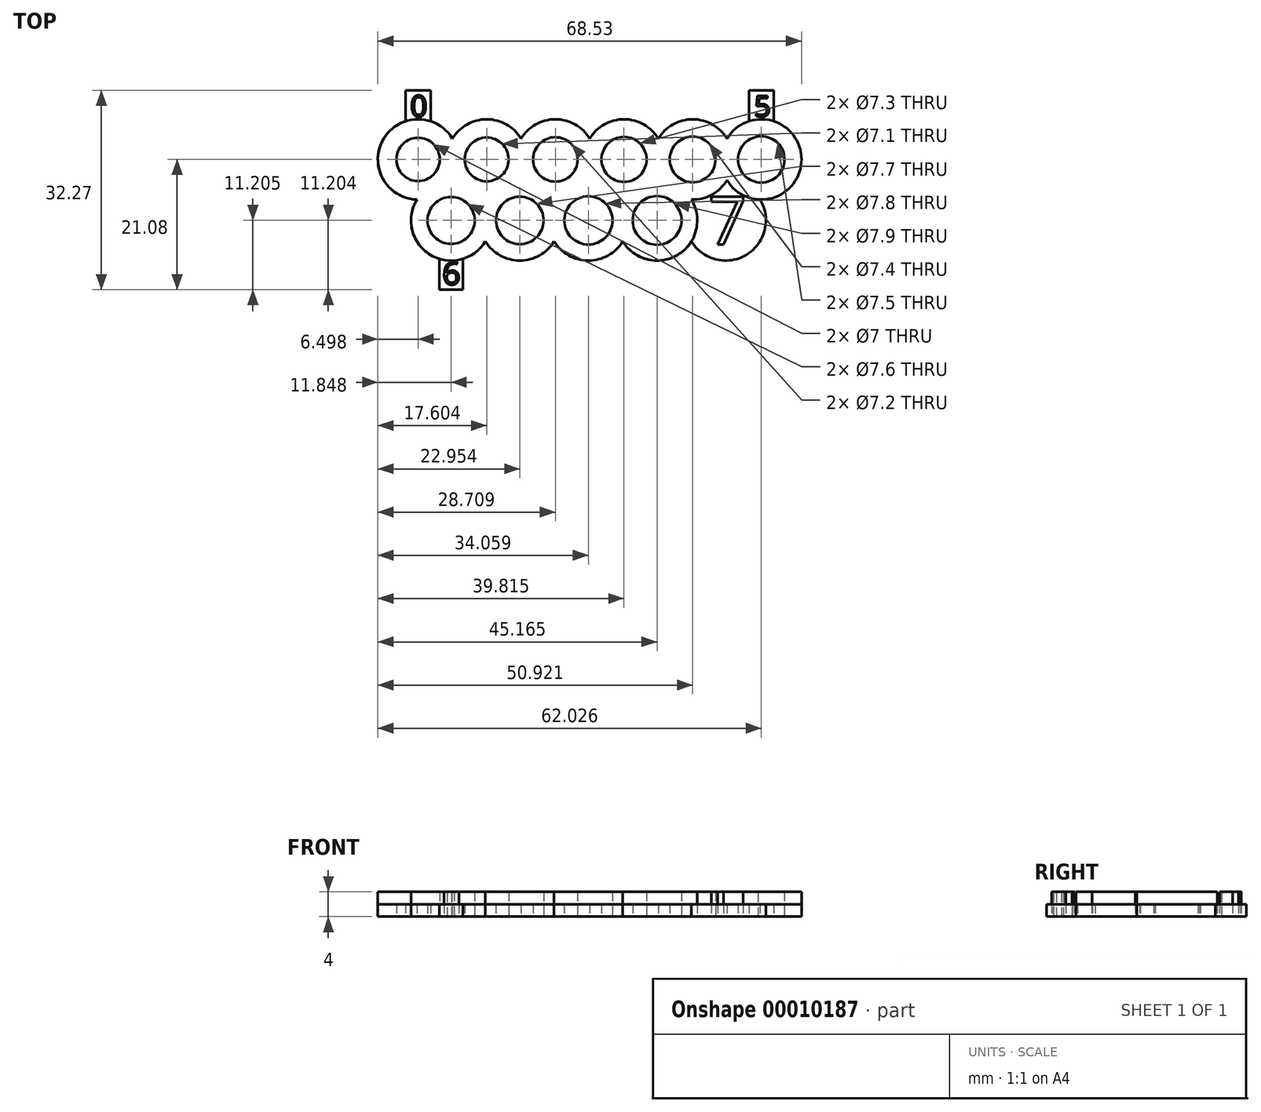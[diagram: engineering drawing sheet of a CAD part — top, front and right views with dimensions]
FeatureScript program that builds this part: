
annotation { "Feature Type Name" : "Feature", "Feature Type Description" : "" }
export const myFeature = defineFeature(function(context is Context, id is Id, definition is map)
    precondition{}
    {
        {
            var Q0;
            Q0=qCreatedBy(makeId("Top.planeOp"),FACE);
            var sketch = newSketch(context, id + "F0", { "sketchPlane" : qUnion([Q0])});
            skCircle(sketch, "E0", {"center": v(-32.25, 0) * mm, "radius": 6.5 * mm});
            skCircle(sketch, "E1", {"center": v(-32.25, 0) * mm, "radius": 3.5 * mm});
            skCircle(sketch, "E2", {"center": v(-21.15, 0) * mm, "radius": 6.5 * mm});
            skCircle(sketch, "E3", {"center": v(-21.15, 0) * mm, "radius": 3.55 * mm});
            skCircle(sketch, "E4", {"center": v(-10.04, 0) * mm, "radius": 6.5 * mm});
            skCircle(sketch, "E5", {"center": v(-10.04, 0) * mm, "radius": 3.6 * mm});
            skCircle(sketch, "E6", {"center": v(1.07, 0) * mm, "radius": 6.5 * mm});
            skCircle(sketch, "E7", {"center": v(1.07, 0) * mm, "radius": 3.65 * mm});
            skCircle(sketch, "E8", {"center": v(12.17, 0) * mm, "radius": 6.5 * mm});
            skCircle(sketch, "E9", {"center": v(12.17, 0) * mm, "radius": 3.7 * mm});
            skCircle(sketch, "E10", {"center": v(23.28, 0) * mm, "radius": 6.5 * mm});
            skCircle(sketch, "E11", {"center": v(23.28, 0) * mm, "radius": 3.75 * mm});
            skCircle(sketch, "E12", {"center": v(-26.9, -9.88) * mm, "radius": 6.5 * mm});
            skCircle(sketch, "E13", {"center": v(-26.9, -9.88) * mm, "radius": 3.8 * mm});
            skCircle(sketch, "E14", {"center": v(-15.8, -9.88) * mm, "radius": 6.5 * mm});
            skCircle(sketch, "E15", {"center": v(-15.8, -9.88) * mm, "radius": 3.85 * mm});
            skCircle(sketch, "E16", {"center": v(-4.7, -9.88) * mm, "radius": 6.5 * mm});
            skCircle(sketch, "E17", {"center": v(-4.7, -9.88) * mm, "radius": 3.9 * mm});
            skCircle(sketch, "E18", {"center": v(6.42, -9.88) * mm, "radius": 6.5 * mm});
            skCircle(sketch, "E19", {"center": v(6.42, -9.88) * mm, "radius": 3.95 * mm});
            skCircle(sketch, "E20", {"center": v(17.52, -9.88) * mm, "radius": 6.5 * mm});
            skPoint(sketch, "E21", {"position": v(-26.7, -3.38) * mm});
            skPoint(sketch, "E22", {"position": v(-15.6, -3.38) * mm});
            skPoint(sketch, "E23", {"position": v(-21.35, -6.5) * mm});
            skPoint(sketch, "E24", {"position": v(-10.24, -6.5) * mm});
            skPoint(sketch, "E25", {"position": v(-4.49, -3.38) * mm});
            skPoint(sketch, "E26", {"position": v(0.86, -6.5) * mm});
            skPoint(sketch, "E27", {"position": v(6.62, -3.38) * mm});
            skPoint(sketch, "E28", {"position": v(11.97, -6.5) * mm});
            skPoint(sketch, "E29", {"position": v(17.72, -3.38) * mm});
            skLineSegment(sketch, "E30.bottom", {"start": v(-34.27, 6.18) * mm, "end": v(-30.23, 6.18) * mm});
            skLineSegment(sketch, "E30.top", {"start": v(-34.27, 11.18) * mm, "end": v(-30.23, 11.18) * mm});
            skLineSegment(sketch, "E30.left", {"start": v(-34.27, 6.18) * mm, "end": v(-34.27, 11.18) * mm});
            skLineSegment(sketch, "E30.right", {"start": v(-30.23, 6.18) * mm, "end": v(-30.23, 11.18) * mm});
            skText(sketch, "E31", { "text": "0", "fontName": "OpenSans-Regular.ttf"});
            skLineSegment(sketch, "E32.left", {"start": v(21.3, 6.19) * mm, "end": v(21.3, 11.19) * mm});
            skLineSegment(sketch, "E32.bottom", {"start": v(21.3, 6.19) * mm, "end": v(25.26, 6.19) * mm});
            skLineSegment(sketch, "E32.right", {"start": v(25.26, 6.19) * mm, "end": v(25.26, 11.19) * mm});
            skLineSegment(sketch, "E32.top", {"start": v(21.3, 11.19) * mm, "end": v(25.26, 11.19) * mm});
            skText(sketch, "E33", { "text": "5", "fontName": "OpenSans-Regular.ttf"});
            skLineSegment(sketch, "E34.left", {"start": v(-28.83, -21.08) * mm, "end": v(-28.83, -16.08) * mm});
            skLineSegment(sketch, "E34.bottom", {"start": v(-28.83, -21.08) * mm, "end": v(-24.97, -21.08) * mm});
            skLineSegment(sketch, "E34.right", {"start": v(-24.97, -21.08) * mm, "end": v(-24.97, -16.08) * mm});
            skLineSegment(sketch, "E34.top", {"start": v(-28.83, -16.08) * mm, "end": v(-24.97, -16.08) * mm});
            skText(sketch, "E35", { "text": "6", "fontName": "OpenSans-Regular.ttf"});
            skText(sketch, "E36", { "text": "7", "fontName": "OpenSans-Regular.ttf"});
            skLineSegment(sketch, "E37", {"start": v(-26.9, -9.88) * mm, "end": v(17.52, -9.88) * mm, "construction": true});
            const initialGuessF0  = {"E31": [-0.0335, 0.00693, 1, 0, 0.00343], "E33": [0.02213, 0.00693, 1, 0, 0.00336], "E35": [-0.02832, -0.02026, 1, 0, 0.00367], "E36": [0.0147, -0.01377, 1, 0, 0.00778]};
            skSetInitialGuess(sketch, initialGuessF0);
            skSolve(sketch);
        }
        {
            var Q0;
            Q0=makeQuery(id+"F0.imprint","IMPRINT",FACE,{"disambiguationData":[TD([[makeQuery(id+"F0.imprint","IMPRINT",EDGE,{"derivedFrom":sQuery(id+"F0.wireOp",EDGE,"E11")}),-1.0]])]});
            var Q1;
            {var subQ0=sQuery(id+"F0.wireOp",EDGE,"E16");var subQ1=sQuery(id+"F0.wireOp",EDGE,"E4");var subQ3=makeQuery(id+"F0.imprint","INTERSECT",VERTEX,{"derivedFrom":[subQ1,sQuery(id+"F0.wireOp",EDGE,"E14"),subQ0]});Q1=makeQuery(id+"F0.imprint","IMPRINT",FACE,{"disambiguationData":[TD([[makeQuery(id+"F0.imprint","IMPRINT",EDGE,{"disambiguationData":[TD([[subQ3,-1.0]])],"derivedFrom":subQ1}),1.0]])]});}
            var Q2;
            {var subQ0=sQuery(id+"F0.wireOp",EDGE,"E18");var subQ1=sQuery(id+"F0.wireOp",EDGE,"E6");var subQ3=makeQuery(id+"F0.imprint","INTERSECT",VERTEX,{"derivedFrom":[subQ1,sQuery(id+"F0.wireOp",EDGE,"E16"),subQ0]});Q2=makeQuery(id+"F0.imprint","IMPRINT",FACE,{"disambiguationData":[TD([[makeQuery(id+"F0.imprint","IMPRINT",EDGE,{"disambiguationData":[TD([[subQ3,-1.0]])],"derivedFrom":subQ1}),1.0]])]});}
            var Q3;
            Q3=makeQuery(id+"F0.imprint","IMPRINT",FACE,{"disambiguationData":[TD([[makeQuery(id+"F0.imprint","IMPRINT",EDGE,{"derivedFrom":sQuery(id+"F0.wireOp",EDGE,"E33.sketch_text.stroke-0")}),-1.0]])]});
            var Q4;
            {var subQ0=sQuery(id+"F0.wireOp",EDGE,"E6");var subQ1=sQuery(id+"F0.wireOp",EDGE,"E4");var subQ3=makeQuery(id+"F0.imprint","INTERSECT",VERTEX,{"derivedFrom":[subQ1,subQ0]});Q4=makeQuery(id+"F0.imprint","IMPRINT",FACE,{"disambiguationData":[TD([[makeQuery(id+"F0.imprint","IMPRINT",EDGE,{"disambiguationData":[TD([[subQ3,1.0]])],"derivedFrom":subQ1}),1.0]])]});}
            var Q5;
            {var subQ0=sQuery(id+"F0.wireOp",EDGE,"E10");var subQ1=sQuery(id+"F0.wireOp",EDGE,"E8");var subQ3=makeQuery(id+"F0.imprint","INTERSECT",VERTEX,{"derivedFrom":[subQ1,subQ0]});Q5=makeQuery(id+"F0.imprint","IMPRINT",FACE,{"disambiguationData":[TD([[makeQuery(id+"F0.imprint","IMPRINT",EDGE,{"disambiguationData":[TD([[subQ3,1.0]])],"derivedFrom":subQ1}),1.0]])]});}
            var Q6;
            {var subQ0=sQuery(id+"F0.wireOp",EDGE,"E12");var subQ1=sQuery(id+"F0.wireOp",EDGE,"E2");var subQ3=makeQuery(id+"F0.imprint","INTERSECT",VERTEX,{"derivedFrom":[sQuery(id+"F0.wireOp",EDGE,"E0"),subQ1,subQ0]});Q6=makeQuery(id+"F0.imprint","IMPRINT",FACE,{"disambiguationData":[TD([[makeQuery(id+"F0.imprint","IMPRINT",EDGE,{"disambiguationData":[TD([[subQ3,-1.0]])],"derivedFrom":subQ1}),1.0]])]});}
            var Q7;
            {var subQ0=sQuery(id+"F0.wireOp",EDGE,"E14");var subQ1=sQuery(id+"F0.wireOp",EDGE,"E12");var subQ3=makeQuery(id+"F0.imprint","INTERSECT",VERTEX,{"derivedFrom":[subQ1,subQ0]});Q7=makeQuery(id+"F0.imprint","IMPRINT",FACE,{"disambiguationData":[TD([[makeQuery(id+"F0.imprint","IMPRINT",EDGE,{"disambiguationData":[TD([[subQ3,-1.0]])],"derivedFrom":subQ1}),1.0]])]});}
            var Q8;
            {var subQ0=sQuery(id+"F0.wireOp",EDGE,"E4");var subQ1=sQuery(id+"F0.wireOp",EDGE,"E2");var subQ3=makeQuery(id+"F0.imprint","INTERSECT",VERTEX,{"derivedFrom":[subQ1,subQ0]});Q8=makeQuery(id+"F0.imprint","IMPRINT",FACE,{"disambiguationData":[TD([[makeQuery(id+"F0.imprint","IMPRINT",EDGE,{"disambiguationData":[TD([[subQ3,1.0]])],"derivedFrom":subQ1}),1.0]])]});}
            var Q9;
            Q9=makeQuery(id+"F0.imprint","IMPRINT",FACE,{"disambiguationData":[TD([[makeQuery(id+"F0.imprint","IMPRINT",EDGE,{"derivedFrom":sQuery(id+"F0.wireOp",EDGE,"E19")}),-1.0]])]});
            var Q10;
            Q10=makeQuery(id+"F0.imprint","IMPRINT",FACE,{"disambiguationData":[TD([[makeQuery(id+"F0.imprint","IMPRINT",EDGE,{"derivedFrom":sQuery(id+"F0.wireOp",EDGE,"E7")}),-1.0]])]});
            var Q11;
            {var subQ0=sQuery(id+"F0.wireOp",EDGE,"E2");var subQ1=sQuery(id+"F0.wireOp",EDGE,"E0");var subQ3=makeQuery(id+"F0.imprint","INTERSECT",VERTEX,{"derivedFrom":[subQ1,subQ0]});Q11=makeQuery(id+"F0.imprint","IMPRINT",FACE,{"disambiguationData":[TD([[makeQuery(id+"F0.imprint","IMPRINT",EDGE,{"disambiguationData":[TD([[subQ3,1.0]])],"derivedFrom":subQ1}),1.0]])]});}
            var Q12;
            Q12=makeQuery(id+"F0.imprint","IMPRINT",FACE,{"disambiguationData":[TD([[makeQuery(id+"F0.imprint","IMPRINT",EDGE,{"derivedFrom":sQuery(id+"F0.wireOp",EDGE,"E36.sketch_text.stroke-0")}),-1.0]])]});
            var Q13;
            {var subQ0=sQuery(id+"F0.wireOp",EDGE,"E20");var subQ1=sQuery(id+"F0.wireOp",EDGE,"E8");var subQ3=makeQuery(id+"F0.imprint","INTERSECT",VERTEX,{"derivedFrom":[subQ1,sQuery(id+"F0.wireOp",EDGE,"E18"),subQ0]});Q13=makeQuery(id+"F0.imprint","IMPRINT",FACE,{"disambiguationData":[TD([[makeQuery(id+"F0.imprint","IMPRINT",EDGE,{"disambiguationData":[TD([[subQ3,-1.0]])],"derivedFrom":subQ1}),1.0]])]});}
            var Q14;
            Q14=makeQuery(id+"F0.imprint","IMPRINT",FACE,{"disambiguationData":[TD([[makeQuery(id+"F0.imprint","IMPRINT",EDGE,{"derivedFrom":sQuery(id+"F0.wireOp",EDGE,"E1")}),-1.0]])]});
            var Q15;
            {var subQ0=sQuery(id+"F0.wireOp",EDGE,"E14");var subQ1=sQuery(id+"F0.wireOp",EDGE,"E4");var subQ3=makeQuery(id+"F0.imprint","INTERSECT",VERTEX,{"derivedFrom":[sQuery(id+"F0.wireOp",EDGE,"E2"),subQ1,subQ0]});Q15=makeQuery(id+"F0.imprint","IMPRINT",FACE,{"disambiguationData":[TD([[makeQuery(id+"F0.imprint","IMPRINT",EDGE,{"disambiguationData":[TD([[subQ3,-1.0]])],"derivedFrom":subQ1}),1.0]])]});}
            var Q16;
            {var subQ0=sQuery(id+"F0.wireOp",EDGE,"E20");var subQ1=sQuery(id+"F0.wireOp",EDGE,"E18");var subQ3=makeQuery(id+"F0.imprint","INTERSECT",VERTEX,{"derivedFrom":[subQ1,subQ0]});Q16=makeQuery(id+"F0.imprint","IMPRINT",FACE,{"disambiguationData":[TD([[makeQuery(id+"F0.imprint","IMPRINT",EDGE,{"disambiguationData":[TD([[subQ3,-1.0]])],"derivedFrom":subQ1}),1.0]])]});}
            var Q17;
            Q17=makeQuery(id+"F0.imprint","IMPRINT",FACE,{"disambiguationData":[TD([[makeQuery(id+"F0.imprint","IMPRINT",EDGE,{"derivedFrom":sQuery(id+"F0.wireOp",EDGE,"E13")}),-1.0]])]});
            var Q18;
            {var subQ0=sQuery(id+"F0.wireOp",EDGE,"E16");var subQ1=sQuery(id+"F0.wireOp",EDGE,"E14");var subQ3=makeQuery(id+"F0.imprint","INTERSECT",VERTEX,{"derivedFrom":[subQ1,subQ0]});Q18=makeQuery(id+"F0.imprint","IMPRINT",FACE,{"disambiguationData":[TD([[makeQuery(id+"F0.imprint","IMPRINT",EDGE,{"disambiguationData":[TD([[subQ3,-1.0]])],"derivedFrom":subQ1}),1.0]])]});}
            var Q19;
            Q19=makeQuery(id+"F0.imprint","IMPRINT",FACE,{"disambiguationData":[TD([[makeQuery(id+"F0.imprint","IMPRINT",EDGE,{"derivedFrom":sQuery(id+"F0.wireOp",EDGE,"E9")}),-1.0]])]});
            var Q20;
            {var subQ0=sQuery(id+"F0.wireOp",EDGE,"E18");var subQ1=sQuery(id+"F0.wireOp",EDGE,"E8");var subQ3=makeQuery(id+"F0.imprint","INTERSECT",VERTEX,{"derivedFrom":[sQuery(id+"F0.wireOp",EDGE,"E6"),subQ1,subQ0]});Q20=makeQuery(id+"F0.imprint","IMPRINT",FACE,{"disambiguationData":[TD([[makeQuery(id+"F0.imprint","IMPRINT",EDGE,{"disambiguationData":[TD([[subQ3,-1.0]])],"derivedFrom":subQ1}),1.0]])]});}
            var Q21;
            Q21=makeQuery(id+"F0.imprint","IMPRINT",FACE,{"disambiguationData":[TD([[makeQuery(id+"F0.imprint","IMPRINT",EDGE,{"derivedFrom":sQuery(id+"F0.wireOp",EDGE,"E3")}),-1.0]])]});
            var Q22;
            {var subQ0=sQuery(id+"F0.wireOp",EDGE,"E18");var subQ1=sQuery(id+"F0.wireOp",EDGE,"E16");var subQ3=makeQuery(id+"F0.imprint","INTERSECT",VERTEX,{"derivedFrom":[subQ1,subQ0]});Q22=makeQuery(id+"F0.imprint","IMPRINT",FACE,{"disambiguationData":[TD([[makeQuery(id+"F0.imprint","IMPRINT",EDGE,{"disambiguationData":[TD([[subQ3,-1.0]])],"derivedFrom":subQ1}),1.0]])]});}
            var Q23;
            {var subQ0=sQuery(id+"F0.wireOp",EDGE,"E8");var subQ1=sQuery(id+"F0.wireOp",EDGE,"E6");var subQ3=makeQuery(id+"F0.imprint","INTERSECT",VERTEX,{"derivedFrom":[subQ1,subQ0]});Q23=makeQuery(id+"F0.imprint","IMPRINT",FACE,{"disambiguationData":[TD([[makeQuery(id+"F0.imprint","IMPRINT",EDGE,{"disambiguationData":[TD([[subQ3,1.0]])],"derivedFrom":subQ1}),1.0]])]});}
            var Q24;
            {var subQ0=sQuery(id+"F0.wireOp",EDGE,"E16");var subQ1=sQuery(id+"F0.wireOp",EDGE,"E6");var subQ3=makeQuery(id+"F0.imprint","INTERSECT",VERTEX,{"derivedFrom":[sQuery(id+"F0.wireOp",EDGE,"E4"),subQ1,subQ0]});Q24=makeQuery(id+"F0.imprint","IMPRINT",FACE,{"disambiguationData":[TD([[makeQuery(id+"F0.imprint","IMPRINT",EDGE,{"disambiguationData":[TD([[subQ3,-1.0]])],"derivedFrom":subQ1}),1.0]])]});}
            var Q25;
            Q25=makeQuery(id+"F0.imprint","IMPRINT",FACE,{"disambiguationData":[TD([[makeQuery(id+"F0.imprint","IMPRINT",EDGE,{"derivedFrom":sQuery(id+"F0.wireOp",EDGE,"E31.sketch_text.stroke-0")}),-1.0]])]});
            var Q26;
            Q26=makeQuery(id+"F0.imprint","IMPRINT",FACE,{"disambiguationData":[TD([[makeQuery(id+"F0.imprint","IMPRINT",EDGE,{"derivedFrom":sQuery(id+"F0.wireOp",EDGE,"E5")}),-1.0]])]});
            var Q27;
            Q27=makeQuery(id+"F0.imprint","IMPRINT",FACE,{"disambiguationData":[TD([[makeQuery(id+"F0.imprint","IMPRINT",EDGE,{"derivedFrom":sQuery(id+"F0.wireOp",EDGE,"E17")}),-1.0]])]});
            var Q28;
            Q28=makeQuery(id+"F0.imprint","IMPRINT",FACE,{"disambiguationData":[TD([[makeQuery(id+"F0.imprint","IMPRINT",EDGE,{"derivedFrom":sQuery(id+"F0.wireOp",EDGE,"E15")}),-1.0]])]});
            var Q29;
            {var subQ0=sQuery(id+"F0.wireOp",EDGE,"E14");var subQ1=sQuery(id+"F0.wireOp",EDGE,"E2");var subQ3=makeQuery(id+"F0.imprint","INTERSECT",VERTEX,{"derivedFrom":[subQ1,sQuery(id+"F0.wireOp",EDGE,"E12"),subQ0]});Q29=makeQuery(id+"F0.imprint","IMPRINT",FACE,{"disambiguationData":[TD([[makeQuery(id+"F0.imprint","IMPRINT",EDGE,{"disambiguationData":[TD([[subQ3,-1.0]])],"derivedFrom":subQ1}),1.0]])]});}
            var Q30;
            {var subQ0=sQuery(id+"F0.wireOp",EDGE,"E20");var subQ1=sQuery(id+"F0.wireOp",EDGE,"E10");var subQ3=makeQuery(id+"F0.imprint","INTERSECT",VERTEX,{"derivedFrom":[subQ1,subQ0]});Q30=makeQuery(id+"F0.imprint","IMPRINT",FACE,{"disambiguationData":[TD([[makeQuery(id+"F0.imprint","IMPRINT",EDGE,{"disambiguationData":[TD([[subQ3,1.0]])],"derivedFrom":subQ1}),1.0]])]});}
            var Q31;
            {var subQ0=sQuery(id+"F0.wireOp",EDGE,"E12");var subQ1=sQuery(id+"F0.wireOp",EDGE,"E0");var subQ3=makeQuery(id+"F0.imprint","INTERSECT",VERTEX,{"derivedFrom":[subQ1,subQ0]});Q31=makeQuery(id+"F0.imprint","IMPRINT",FACE,{"disambiguationData":[TD([[makeQuery(id+"F0.imprint","IMPRINT",EDGE,{"disambiguationData":[TD([[subQ3,-1.0]])],"derivedFrom":subQ1}),1.0]])]});}
            var Q32;
            Q32=makeQuery(id+"F0.imprint","IMPRINT",FACE,{"disambiguationData":[TD([[makeQuery(id+"F0.imprint","IMPRINT",EDGE,{"derivedFrom":sQuery(id+"F0.wireOp",EDGE,"E35.sketch_text.stroke-0")}),-1.0]])]});
            var Q33;
            {var subQ0=sQuery(id+"F0.wireOp",EDGE,"E34.top");Q33=makeQuery(id+"F0.imprint","IMPRINT",FACE,{"disambiguationData":[TD([[makeQuery(id+"F0.imprint","IMPRINT",EDGE,{"derivedFrom":subQ0}),-1.0]])]});}
            var Q34;
            {var subQ0=sQuery(id+"F0.wireOp",EDGE,"E30.bottom");Q34=makeQuery(id+"F0.imprint","IMPRINT",FACE,{"disambiguationData":[TD([[makeQuery(id+"F0.imprint","IMPRINT",EDGE,{"derivedFrom":subQ0}),1.0]])]});}
            var Q35;
            {var subQ0=sQuery(id+"F0.wireOp",EDGE,"E32.bottom");Q35=makeQuery(id+"F0.imprint","IMPRINT",FACE,{"disambiguationData":[TD([[makeQuery(id+"F0.imprint","IMPRINT",EDGE,{"derivedFrom":subQ0}),1.0]])]});}
            extrude(context, id + "F1", {"entities" : qUnion([Q0, Q1, Q2, Q3, Q4, Q5, Q6, Q7, Q8, Q9, Q10, Q11, Q12, Q13, Q14, Q15, Q16, Q17, Q18, Q19, Q20, Q21, Q22, Q23, Q24, Q25, Q26, Q27, Q28, Q29, Q30, Q31, Q32, Q33, Q34, Q35]), "depth" : 4 * mm});
        }
        {
            var Q0;
            Q0=makeQuery(id+"F0.imprint","IMPRINT",FACE,{"disambiguationData":[TD([[makeQuery(id+"F0.imprint","IMPRINT",EDGE,{"derivedFrom":sQuery(id+"F0.wireOp",EDGE,"E13")}),-1.0]])]});
            var Q1;
            {var subQ0=sQuery(id+"F0.wireOp",EDGE,"E16");var subQ1=sQuery(id+"F0.wireOp",EDGE,"E6");var subQ3=makeQuery(id+"F0.imprint","INTERSECT",VERTEX,{"derivedFrom":[sQuery(id+"F0.wireOp",EDGE,"E4"),subQ1,subQ0]});Q1=makeQuery(id+"F0.imprint","IMPRINT",FACE,{"disambiguationData":[TD([[makeQuery(id+"F0.imprint","IMPRINT",EDGE,{"disambiguationData":[TD([[subQ3,-1.0]])],"derivedFrom":subQ1}),1.0]])]});}
            var Q2;
            {var subQ0=sQuery(id+"F0.wireOp",EDGE,"E8");var subQ1=sQuery(id+"F0.wireOp",EDGE,"E6");var subQ3=makeQuery(id+"F0.imprint","INTERSECT",VERTEX,{"derivedFrom":[subQ1,subQ0]});Q2=makeQuery(id+"F0.imprint","IMPRINT",FACE,{"disambiguationData":[TD([[makeQuery(id+"F0.imprint","IMPRINT",EDGE,{"disambiguationData":[TD([[subQ3,1.0]])],"derivedFrom":subQ1}),1.0]])]});}
            var Q3;
            {var subQ0=sQuery(id+"F0.wireOp",EDGE,"E18");var subQ1=sQuery(id+"F0.wireOp",EDGE,"E6");var subQ3=makeQuery(id+"F0.imprint","INTERSECT",VERTEX,{"derivedFrom":[subQ1,sQuery(id+"F0.wireOp",EDGE,"E16"),subQ0]});Q3=makeQuery(id+"F0.imprint","IMPRINT",FACE,{"disambiguationData":[TD([[makeQuery(id+"F0.imprint","IMPRINT",EDGE,{"disambiguationData":[TD([[subQ3,-1.0]])],"derivedFrom":subQ1}),1.0]])]});}
            var Q4;
            {var subQ0=sQuery(id+"F0.wireOp",EDGE,"E14");var subQ1=sQuery(id+"F0.wireOp",EDGE,"E2");var subQ3=makeQuery(id+"F0.imprint","INTERSECT",VERTEX,{"derivedFrom":[subQ1,sQuery(id+"F0.wireOp",EDGE,"E12"),subQ0]});Q4=makeQuery(id+"F0.imprint","IMPRINT",FACE,{"disambiguationData":[TD([[makeQuery(id+"F0.imprint","IMPRINT",EDGE,{"disambiguationData":[TD([[subQ3,-1.0]])],"derivedFrom":subQ1}),1.0]])]});}
            var Q5;
            Q5=makeQuery(id+"F0.imprint","IMPRINT",FACE,{"disambiguationData":[TD([[makeQuery(id+"F0.imprint","IMPRINT",EDGE,{"derivedFrom":sQuery(id+"F0.wireOp",EDGE,"E1")}),-1.0]])]});
            var Q6;
            Q6=makeQuery(id+"F0.imprint","IMPRINT",FACE,{"disambiguationData":[TD([[makeQuery(id+"F0.imprint","IMPRINT",EDGE,{"derivedFrom":sQuery(id+"F0.wireOp",EDGE,"E11")}),-1.0]])]});
            var Q7;
            {var subQ0=sQuery(id+"F0.wireOp",EDGE,"E16");var subQ1=sQuery(id+"F0.wireOp",EDGE,"E4");var subQ3=makeQuery(id+"F0.imprint","INTERSECT",VERTEX,{"derivedFrom":[subQ1,sQuery(id+"F0.wireOp",EDGE,"E14"),subQ0]});Q7=makeQuery(id+"F0.imprint","IMPRINT",FACE,{"disambiguationData":[TD([[makeQuery(id+"F0.imprint","IMPRINT",EDGE,{"disambiguationData":[TD([[subQ3,-1.0]])],"derivedFrom":subQ1}),1.0]])]});}
            var Q8;
            Q8=makeQuery(id+"F0.imprint","IMPRINT",FACE,{"disambiguationData":[TD([[makeQuery(id+"F0.imprint","IMPRINT",EDGE,{"derivedFrom":sQuery(id+"F0.wireOp",EDGE,"E36.sketch_text.stroke-0")}),1.0]])]});
            var Q9;
            {var subQ0=sQuery(id+"F0.wireOp",EDGE,"E18");var subQ1=sQuery(id+"F0.wireOp",EDGE,"E16");var subQ3=makeQuery(id+"F0.imprint","INTERSECT",VERTEX,{"derivedFrom":[subQ1,subQ0]});Q9=makeQuery(id+"F0.imprint","IMPRINT",FACE,{"disambiguationData":[TD([[makeQuery(id+"F0.imprint","IMPRINT",EDGE,{"disambiguationData":[TD([[subQ3,-1.0]])],"derivedFrom":subQ1}),1.0]])]});}
            var Q10;
            Q10=makeQuery(id+"F0.imprint","IMPRINT",FACE,{"disambiguationData":[TD([[makeQuery(id+"F0.imprint","IMPRINT",EDGE,{"derivedFrom":sQuery(id+"F0.wireOp",EDGE,"E9")}),-1.0]])]});
            var Q11;
            Q11=makeQuery(id+"F0.imprint","IMPRINT",FACE,{"disambiguationData":[TD([[makeQuery(id+"F0.imprint","IMPRINT",EDGE,{"derivedFrom":sQuery(id+"F0.wireOp",EDGE,"E35.sketch_text.stroke-15")}),1.0]])]});
            var Q12;
            {var subQ0=sQuery(id+"F0.wireOp",EDGE,"E16");var subQ1=sQuery(id+"F0.wireOp",EDGE,"E14");var subQ3=makeQuery(id+"F0.imprint","INTERSECT",VERTEX,{"derivedFrom":[subQ1,subQ0]});Q12=makeQuery(id+"F0.imprint","IMPRINT",FACE,{"disambiguationData":[TD([[makeQuery(id+"F0.imprint","IMPRINT",EDGE,{"disambiguationData":[TD([[subQ3,-1.0]])],"derivedFrom":subQ1}),1.0]])]});}
            var Q13;
            Q13=makeQuery(id+"F0.imprint","IMPRINT",FACE,{"disambiguationData":[TD([[makeQuery(id+"F0.imprint","IMPRINT",EDGE,{"derivedFrom":sQuery(id+"F0.wireOp",EDGE,"E36.sketch_text.stroke-0")}),-1.0]])]});
            var Q14;
            {var subQ1=sQuery(id+"F0.wireOp",EDGE,"E34.left");Q14=makeQuery(id+"F0.imprint","IMPRINT",FACE,{"disambiguationData":[TD([[makeQuery(id+"F0.imprint","IMPRINT",EDGE,{"derivedFrom":subQ1}),-1.0]])]});}
            var Q15;
            Q15=makeQuery(id+"F0.imprint","IMPRINT",FACE,{"disambiguationData":[TD([[makeQuery(id+"F0.imprint","IMPRINT",EDGE,{"derivedFrom":sQuery(id+"F0.wireOp",EDGE,"E15")}),-1.0]])]});
            var Q16;
            Q16=makeQuery(id+"F0.imprint","IMPRINT",FACE,{"disambiguationData":[TD([[makeQuery(id+"F0.imprint","IMPRINT",EDGE,{"derivedFrom":sQuery(id+"F0.wireOp",EDGE,"E3")}),-1.0]])]});
            var Q17;
            Q17=makeQuery(id+"F0.imprint","IMPRINT",FACE,{"disambiguationData":[TD([[makeQuery(id+"F0.imprint","IMPRINT",EDGE,{"derivedFrom":sQuery(id+"F0.wireOp",EDGE,"E7")}),-1.0]])]});
            var Q18;
            {var subQ0=sQuery(id+"F0.wireOp",EDGE,"E2");var subQ1=sQuery(id+"F0.wireOp",EDGE,"E0");var subQ3=makeQuery(id+"F0.imprint","INTERSECT",VERTEX,{"derivedFrom":[subQ1,subQ0]});Q18=makeQuery(id+"F0.imprint","IMPRINT",FACE,{"disambiguationData":[TD([[makeQuery(id+"F0.imprint","IMPRINT",EDGE,{"disambiguationData":[TD([[subQ3,1.0]])],"derivedFrom":subQ1}),1.0]])]});}
            var Q19;
            {var subQ0=sQuery(id+"F0.wireOp",EDGE,"E18");var subQ1=sQuery(id+"F0.wireOp",EDGE,"E8");var subQ3=makeQuery(id+"F0.imprint","INTERSECT",VERTEX,{"derivedFrom":[sQuery(id+"F0.wireOp",EDGE,"E6"),subQ1,subQ0]});Q19=makeQuery(id+"F0.imprint","IMPRINT",FACE,{"disambiguationData":[TD([[makeQuery(id+"F0.imprint","IMPRINT",EDGE,{"disambiguationData":[TD([[subQ3,-1.0]])],"derivedFrom":subQ1}),1.0]])]});}
            var Q20;
            {var subQ3=sQuery(id+"F0.wireOp",EDGE,"E32.left");Q20=makeQuery(id+"F0.imprint","IMPRINT",FACE,{"disambiguationData":[TD([[makeQuery(id+"F0.imprint","IMPRINT",EDGE,{"derivedFrom":subQ3}),-1.0]])]});}
            var Q21;
            {var subQ0=sQuery(id+"F0.wireOp",EDGE,"E12");var subQ1=sQuery(id+"F0.wireOp",EDGE,"E0");var subQ3=makeQuery(id+"F0.imprint","INTERSECT",VERTEX,{"derivedFrom":[subQ1,subQ0]});Q21=makeQuery(id+"F0.imprint","IMPRINT",FACE,{"disambiguationData":[TD([[makeQuery(id+"F0.imprint","IMPRINT",EDGE,{"disambiguationData":[TD([[subQ3,-1.0]])],"derivedFrom":subQ1}),1.0]])]});}
            var Q22;
            {var subQ0=sQuery(id+"F0.wireOp",EDGE,"E12");var subQ1=sQuery(id+"F0.wireOp",EDGE,"E2");var subQ3=makeQuery(id+"F0.imprint","INTERSECT",VERTEX,{"derivedFrom":[sQuery(id+"F0.wireOp",EDGE,"E0"),subQ1,subQ0]});Q22=makeQuery(id+"F0.imprint","IMPRINT",FACE,{"disambiguationData":[TD([[makeQuery(id+"F0.imprint","IMPRINT",EDGE,{"disambiguationData":[TD([[subQ3,-1.0]])],"derivedFrom":subQ1}),1.0]])]});}
            var Q23;
            {var subQ0=sQuery(id+"F0.wireOp",EDGE,"E20");var subQ1=sQuery(id+"F0.wireOp",EDGE,"E8");var subQ3=makeQuery(id+"F0.imprint","INTERSECT",VERTEX,{"derivedFrom":[subQ1,sQuery(id+"F0.wireOp",EDGE,"E18"),subQ0]});Q23=makeQuery(id+"F0.imprint","IMPRINT",FACE,{"disambiguationData":[TD([[makeQuery(id+"F0.imprint","IMPRINT",EDGE,{"disambiguationData":[TD([[subQ3,-1.0]])],"derivedFrom":subQ1}),1.0]])]});}
            var Q24;
            {var subQ0=sQuery(id+"F0.wireOp",EDGE,"E10");var subQ1=sQuery(id+"F0.wireOp",EDGE,"E8");var subQ3=makeQuery(id+"F0.imprint","INTERSECT",VERTEX,{"derivedFrom":[subQ1,subQ0]});Q24=makeQuery(id+"F0.imprint","IMPRINT",FACE,{"disambiguationData":[TD([[makeQuery(id+"F0.imprint","IMPRINT",EDGE,{"disambiguationData":[TD([[subQ3,1.0]])],"derivedFrom":subQ1}),1.0]])]});}
            var Q25;
            {var subQ0=sQuery(id+"F0.wireOp",EDGE,"E20");var subQ1=sQuery(id+"F0.wireOp",EDGE,"E10");var subQ3=makeQuery(id+"F0.imprint","INTERSECT",VERTEX,{"derivedFrom":[subQ1,subQ0]});Q25=makeQuery(id+"F0.imprint","IMPRINT",FACE,{"disambiguationData":[TD([[makeQuery(id+"F0.imprint","IMPRINT",EDGE,{"disambiguationData":[TD([[subQ3,1.0]])],"derivedFrom":subQ1}),1.0]])]});}
            var Q26;
            Q26=makeQuery(id+"F0.imprint","IMPRINT",FACE,{"disambiguationData":[TD([[makeQuery(id+"F0.imprint","IMPRINT",EDGE,{"derivedFrom":sQuery(id+"F0.wireOp",EDGE,"E30.top")}),-1.0]])]});
            var Q27;
            {var subQ0=sQuery(id+"F0.wireOp",EDGE,"E20");var subQ1=sQuery(id+"F0.wireOp",EDGE,"E18");var subQ3=makeQuery(id+"F0.imprint","INTERSECT",VERTEX,{"derivedFrom":[subQ1,subQ0]});Q27=makeQuery(id+"F0.imprint","IMPRINT",FACE,{"disambiguationData":[TD([[makeQuery(id+"F0.imprint","IMPRINT",EDGE,{"disambiguationData":[TD([[subQ3,-1.0]])],"derivedFrom":subQ1}),1.0]])]});}
            var Q28;
            Q28=makeQuery(id+"F0.imprint","IMPRINT",FACE,{"disambiguationData":[TD([[makeQuery(id+"F0.imprint","IMPRINT",EDGE,{"derivedFrom":sQuery(id+"F0.wireOp",EDGE,"E17")}),-1.0]])]});
            var Q29;
            {var subQ0=sQuery(id+"F0.wireOp",EDGE,"E14");var subQ1=sQuery(id+"F0.wireOp",EDGE,"E12");var subQ3=makeQuery(id+"F0.imprint","INTERSECT",VERTEX,{"derivedFrom":[subQ1,subQ0]});Q29=makeQuery(id+"F0.imprint","IMPRINT",FACE,{"disambiguationData":[TD([[makeQuery(id+"F0.imprint","IMPRINT",EDGE,{"disambiguationData":[TD([[subQ3,-1.0]])],"derivedFrom":subQ1}),1.0]])]});}
            var Q30;
            Q30=makeQuery(id+"F0.imprint","IMPRINT",FACE,{"disambiguationData":[TD([[makeQuery(id+"F0.imprint","IMPRINT",EDGE,{"derivedFrom":sQuery(id+"F0.wireOp",EDGE,"E19")}),-1.0]])]});
            var Q31;
            {var subQ0=sQuery(id+"F0.wireOp",EDGE,"E4");var subQ1=sQuery(id+"F0.wireOp",EDGE,"E2");var subQ3=makeQuery(id+"F0.imprint","INTERSECT",VERTEX,{"derivedFrom":[subQ1,subQ0]});Q31=makeQuery(id+"F0.imprint","IMPRINT",FACE,{"disambiguationData":[TD([[makeQuery(id+"F0.imprint","IMPRINT",EDGE,{"disambiguationData":[TD([[subQ3,1.0]])],"derivedFrom":subQ1}),1.0]])]});}
            var Q32;
            Q32=makeQuery(id+"F0.imprint","IMPRINT",FACE,{"disambiguationData":[TD([[makeQuery(id+"F0.imprint","IMPRINT",EDGE,{"derivedFrom":sQuery(id+"F0.wireOp",EDGE,"E33.sketch_text.stroke-0")}),-1.0]])]});
            var Q33;
            Q33=makeQuery(id+"F0.imprint","IMPRINT",FACE,{"disambiguationData":[TD([[makeQuery(id+"F0.imprint","IMPRINT",EDGE,{"derivedFrom":sQuery(id+"F0.wireOp",EDGE,"E31.sketch_text.stroke-8")}),1.0]])]});
            var Q34;
            {var subQ0=sQuery(id+"F0.wireOp",EDGE,"E14");var subQ1=sQuery(id+"F0.wireOp",EDGE,"E4");var subQ3=makeQuery(id+"F0.imprint","INTERSECT",VERTEX,{"derivedFrom":[sQuery(id+"F0.wireOp",EDGE,"E2"),subQ1,subQ0]});Q34=makeQuery(id+"F0.imprint","IMPRINT",FACE,{"disambiguationData":[TD([[makeQuery(id+"F0.imprint","IMPRINT",EDGE,{"disambiguationData":[TD([[subQ3,-1.0]])],"derivedFrom":subQ1}),1.0]])]});}
            var Q35;
            Q35=makeQuery(id+"F0.imprint","IMPRINT",FACE,{"disambiguationData":[TD([[makeQuery(id+"F0.imprint","IMPRINT",EDGE,{"derivedFrom":sQuery(id+"F0.wireOp",EDGE,"E31.sketch_text.stroke-0")}),-1.0]])]});
            var Q36;
            {var subQ0=sQuery(id+"F0.wireOp",EDGE,"E6");var subQ1=sQuery(id+"F0.wireOp",EDGE,"E4");var subQ3=makeQuery(id+"F0.imprint","INTERSECT",VERTEX,{"derivedFrom":[subQ1,subQ0]});Q36=makeQuery(id+"F0.imprint","IMPRINT",FACE,{"disambiguationData":[TD([[makeQuery(id+"F0.imprint","IMPRINT",EDGE,{"disambiguationData":[TD([[subQ3,1.0]])],"derivedFrom":subQ1}),1.0]])]});}
            var Q37;
            Q37=makeQuery(id+"F0.imprint","IMPRINT",FACE,{"disambiguationData":[TD([[makeQuery(id+"F0.imprint","IMPRINT",EDGE,{"derivedFrom":sQuery(id+"F0.wireOp",EDGE,"E5")}),-1.0]])]});
            var Q38;
            Q38=makeQuery(id+"F0.imprint","IMPRINT",FACE,{"disambiguationData":[TD([[makeQuery(id+"F0.imprint","IMPRINT",EDGE,{"derivedFrom":sQuery(id+"F0.wireOp",EDGE,"E35.sketch_text.stroke-0")}),-1.0]])]});
            var Q39;
            {var subQ0=sQuery(id+"F0.wireOp",EDGE,"E34.top");Q39=makeQuery(id+"F0.imprint","IMPRINT",FACE,{"disambiguationData":[TD([[makeQuery(id+"F0.imprint","IMPRINT",EDGE,{"derivedFrom":subQ0}),-1.0]])]});}
            var Q40;
            {var subQ0=sQuery(id+"F0.wireOp",EDGE,"E30.bottom");Q40=makeQuery(id+"F0.imprint","IMPRINT",FACE,{"disambiguationData":[TD([[makeQuery(id+"F0.imprint","IMPRINT",EDGE,{"derivedFrom":subQ0}),1.0]])]});}
            var Q41;
            {var subQ0=sQuery(id+"F0.wireOp",EDGE,"E32.bottom");Q41=makeQuery(id+"F0.imprint","IMPRINT",FACE,{"disambiguationData":[TD([[makeQuery(id+"F0.imprint","IMPRINT",EDGE,{"derivedFrom":subQ0}),1.0]])]});}
            extrude(context, id + "F2", {"entities" : qUnion([Q0, Q1, Q2, Q3, Q4, Q5, Q6, Q7, Q8, Q9, Q10, Q11, Q12, Q13, Q14, Q15, Q16, Q17, Q18, Q19, Q20, Q21, Q22, Q23, Q24, Q25, Q26, Q27, Q28, Q29, Q30, Q31, Q32, Q33, Q34, Q35, Q36, Q37, Q38, Q39, Q40, Q41]), "depth" : 2 * mm});
        }
    });
